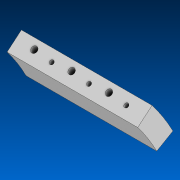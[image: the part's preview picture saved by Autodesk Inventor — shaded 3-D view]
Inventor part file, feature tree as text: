
AUTODESK INVENTOR PART (.ipt)
format: ipt  version: 2022 (Build 260153000, 153)  size: 141,312 bytes
history: native  units: in
note: dims shown in document units (in); Inventor stores cm internally (conversion verified against a paired STEP export)
features: sketch x5, extrude x2, hole x2, pattern_linear x2, plane x1
ambient origin geometry x8: Origin, YZ Plane, XZ Plane, XY Plane, X Axis, Y Axis, Z Axis, Center Point
bodies: Solid1 (feature_tree)
feature tree (12):
  extrude  "Extrusion1"  Depth=10.9074in
  hole  "Hole2"  [1 undecoded]
  pattern_linear  "Rectangular Pattern2"  Count1=3 Spacing1=2.0in
  sketch  "Sketch5"  dims[d6=7.0in d7=0.0in]
  hole  "Hole3"  [1 undecoded]
  plane  "Work Plane1"
  extrude  "Extrusion2"  Depth=1.0in
  pattern_linear  "Rectangular Pattern3"  Spacing1=0.32in  [1 undecoded]
  sketch  "Sketch1"  dims[d1=10.9074in d2=0.2749in]
  sketch  "Sketch3"  dims[d4=1.0in d5=1.0in]
  sketch  "Sketch6"  dims[d17=1.0in]
  sketch  "Sketch7"  dims[d18=0.5in d19=0.175in d20=0.75in d21=0.22in d22=0.325in d23=0.5635in d24=1.5in d25=0.0in d29=1.1811in d31=2.0in d32=30.0deg d33=1.0in d36=0.175in d37=0.75in d38=0.22in d39=0.325in d40=0.5635in d41=1.5in d42=0.0in d44=0.32in d45=0.0in d46=0.0in d47=1.1811in d49=2.0in d50=1.0in d51=0.5115in d52=-1.0in d53=0.0344in]
note: 3 required parameter values undecoded (feature->parameter linkage not recoverable at this tier; creation-order binding heuristic only, values carry confidence <= 0.55)
